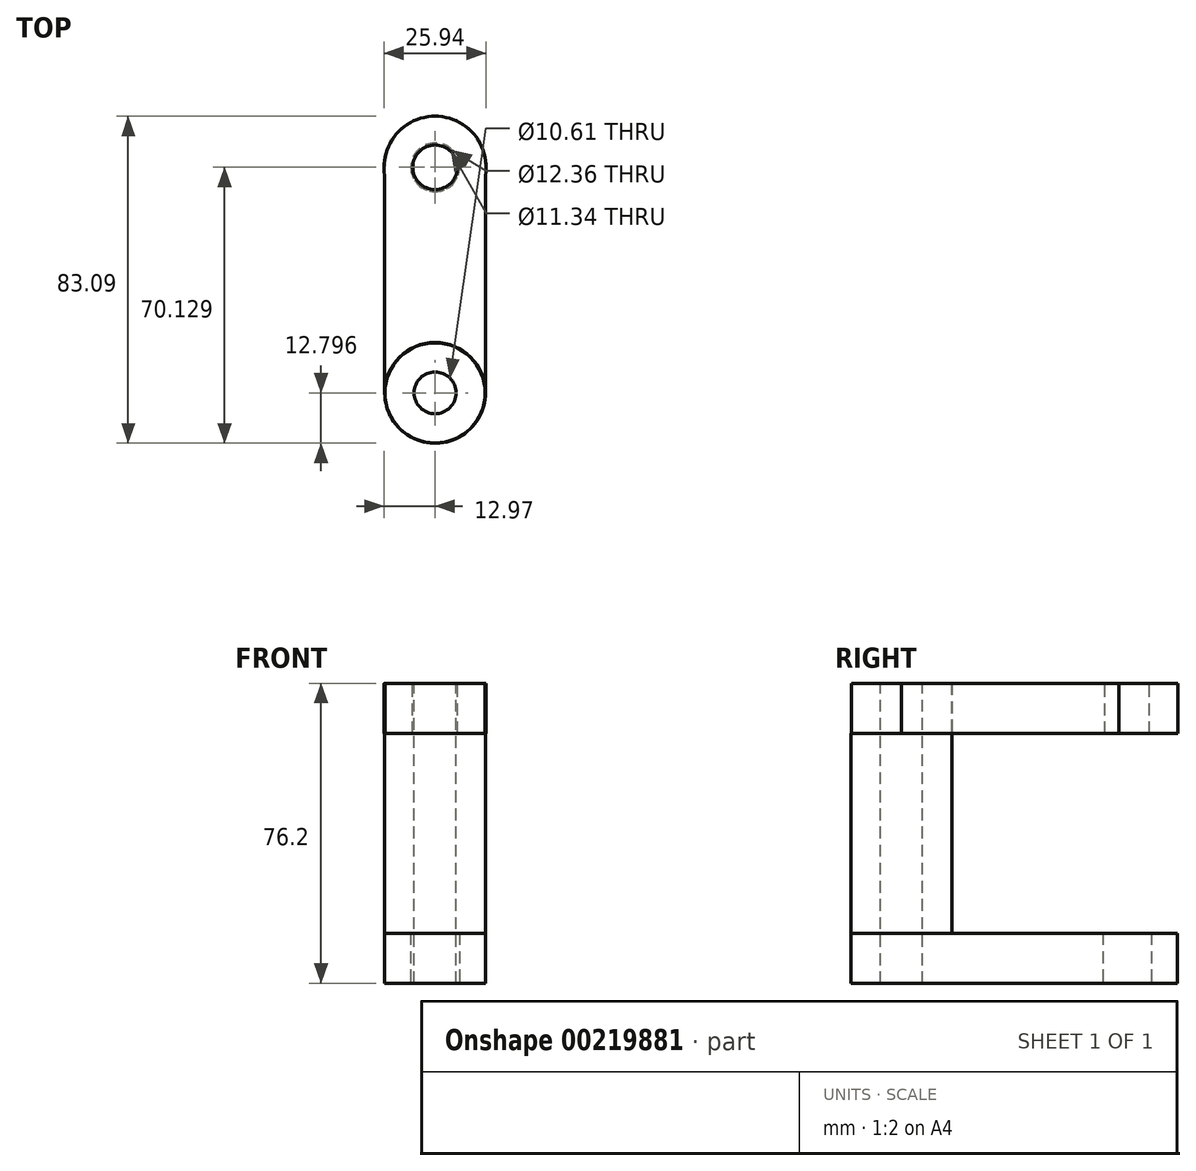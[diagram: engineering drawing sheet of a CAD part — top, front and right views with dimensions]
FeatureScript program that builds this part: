
annotation { "Feature Type Name" : "Feature", "Feature Type Description" : "" }
export const myFeature = defineFeature(function(context is Context, id is Id, definition is map)
    precondition{}
    {
        {
            var Q0;
            Q0=qCreatedBy(makeId("Top.planeOp"),FACE);
            var sketch = newSketch(context, id + "F0", { "sketchPlane" : qUnion([Q0])});
            skCircle(sketch, "E0", {"center": v(0, 31.52) * mm, "radius": 12.77 * mm});
            skLineSegment(sketch, "E1", {"start": v(12.77, 31.52) * mm, "end": v(12.77, -25.81) * mm});
            skLineSegment(sketch, "E2", {"start": v(-12.77, 31.52) * mm, "end": v(-12.77, -25.81) * mm});
            skCircle(sketch, "E3", {"center": v(0, -25.81) * mm, "radius": 12.77 * mm});
            skSolve(sketch);
        }
        {
            var Q0;
            Q0 = qSketchRegion(id + "F0", true);
            extrude(context, id + "F1", {"entities" : qUnion([Q0]), "oppositeDirection" : true, "depth" : 12.7 * mm});
        }
        {
            var Q0;
            Q0=makeQuery(id+"F1.opExtrude","CAP_FACE",FACE,{"disambiguationData":[OSD([sQuery(id+"F0.wireOp",EDGE,"E0"),sQuery(id+"F0.wireOp",EDGE,"E1"),sQuery(id+"F0.wireOp",EDGE,"E2"),sQuery(id+"F0.wireOp",EDGE,"E3")])],"isStart":true});
            var sketch = newSketch(context, id + "F2", { "sketchPlane" : qUnion([Q0])});
            skCircle(sketch, "E4", {"center": v(0, -25.81) * mm, "radius": 12.8 * mm});
            skSolve(sketch);
        }
        {
            var Q0;
            Q0 = qSketchRegion(id + "F2", true);
            extrude(context, id + "F3", {"entities" : qUnion([Q0]), "operationType" : NewBodyOperationType.ADD, "depth" : 50.8 * mm});
        }
        {
            var Q0;
            Q0=makeQuery(id+"F3.opExtrude","CAP_FACE",FACE,{"disambiguationData":[OSD([sQuery(id+"F2.wireOp",EDGE,"E4")])],"isStart":false});
            var sketch = newSketch(context, id + "F4", { "sketchPlane" : qUnion([Q0])});
            skCircle(sketch, "E5", {"center": v(0, -25.81) * mm, "radius": 12.73 * mm});
            skLineSegment(sketch, "E6", {"start": v(12.8, -25.81) * mm, "end": v(12.8, 31.52) * mm});
            skLineSegment(sketch, "E7", {"start": v(-12.8, -25.81) * mm, "end": v(-12.8, 31.52) * mm});
            skCircle(sketch, "E8", {"center": v(0, 31.52) * mm, "radius": 12.97 * mm});
            skSolve(sketch);
        }
        {
            var Q0;
            {var subQ0=sQuery(id+"F4.wireOp",EDGE,"E6");var subQ1=makeQuery(id+"F3.opExtrude","CAP_EDGE",EDGE,{"disambiguationData":[OSD([sQuery(id+"F2.wireOp",EDGE,"E4")])],"isStart":false});var subQ2=makeQuery(id+"F4.imprint","INTERSECT",VERTEX,{"derivedFrom":[subQ1,subQ0]});Q0=makeQuery(id+"F4.imprint","IMPRINT",FACE,{"disambiguationData":[TD([[makeQuery(id+"F4.imprint","IMPRINT",EDGE,{"disambiguationData":[TD([[subQ2,-1.0]])],"derivedFrom":subQ0}),1.0]])]});}
            var Q1;
            {var subQ0=sQuery(id+"F4.wireOp",EDGE,"E8");var subQ1=makeQuery(id+"F4.imprint","INTERSECT",VERTEX,{"derivedFrom":[sQuery(id+"F4.wireOp",EDGE,"E6"),subQ0]});Q1=makeQuery(id+"F4.imprint","IMPRINT",FACE,{"disambiguationData":[TD([[makeQuery(id+"F4.imprint","IMPRINT",EDGE,{"disambiguationData":[TD([[subQ1,1.0]])],"derivedFrom":subQ0}),1.0]])]});}
            var Q2;
            Q2=makeQuery(id+"F4.imprint","IMPRINT",FACE,{"disambiguationData":[TD([[makeQuery(id+"F4.imprint","IMPRINT",EDGE,{"derivedFrom":sQuery(id+"F4.wireOp",EDGE,"E5")}),1.0]])]});
            extrude(context, id + "F5", {"entities" : qUnion([Q0, Q1, Q2]), "operationType" : NewBodyOperationType.ADD, "depth" : 12.7 * mm});
        }
        {
            var Q0;
            Q0=makeQuery(id+"F5.opExtrude","CAP_FACE",FACE,{"disambiguationData":[OSD([sQuery(id+"F4.wireOp",EDGE,"E5")])],"isStart":false});
            var sketch = newSketch(context, id + "F6", { "sketchPlane" : qUnion([Q0])});
            skCircle(sketch, "E9", {"center": v(0, -25.81) * mm, "radius": 5.3 * mm});
            skSolve(sketch);
        }
        {
            var Q0;
            Q0 = qSketchRegion(id + "F6", true);
            extrude(context, id + "F7", {"entities" : qUnion([Q0]), "operationType" : NewBodyOperationType.REMOVE, "oppositeDirection" : true, "depth" : 101.6 * mm});
        }
        {
            var Q0;
            Q0=makeQuery(id+"F5.opExtrude","CAP_FACE",FACE,{"disambiguationData":[OSD([sQuery(id+"F2.wireOp",EDGE,"E4"),sQuery(id+"F4.wireOp",EDGE,"E6"),sQuery(id+"F4.wireOp",EDGE,"E7"),sQuery(id+"F4.wireOp",EDGE,"E8")])],"isStart":false});
            var sketch = newSketch(context, id + "F8", { "sketchPlane" : qUnion([Q0])});
            skCircle(sketch, "E10", {"center": v(0, 31.52) * mm, "radius": 5.67 * mm});
            skSolve(sketch);
        }
        {
            var Q0;
            Q0 = qSketchRegion(id + "F8", true);
            extrude(context, id + "F9", {"entities" : qUnion([Q0]), "operationType" : NewBodyOperationType.REMOVE, "oppositeDirection" : true, "depth" : 101.6 * mm});
        }
        {
            var Q0;
            Q0=makeQuery(id+"F1.opExtrude","CAP_FACE",FACE,{"disambiguationData":[OSD([sQuery(id+"F0.wireOp",EDGE,"E0"),sQuery(id+"F0.wireOp",EDGE,"E1"),sQuery(id+"F0.wireOp",EDGE,"E2"),sQuery(id+"F0.wireOp",EDGE,"E3")])],"isStart":false});
            var sketch = newSketch(context, id + "F10", { "sketchPlane" : qUnion([Q0])});
            skCircle(sketch, "E11", {"center": v(0, -31.52) * mm, "radius": 6.18 * mm});
            skSolve(sketch);
        }
        {
            var Q0;
            Q0 = qSketchRegion(id + "F10", true);
            extrude(context, id + "F11", {"entities" : qUnion([Q0]), "operationType" : NewBodyOperationType.REMOVE, "oppositeDirection" : true, "depth" : 25.4 * mm});
        }
    });
